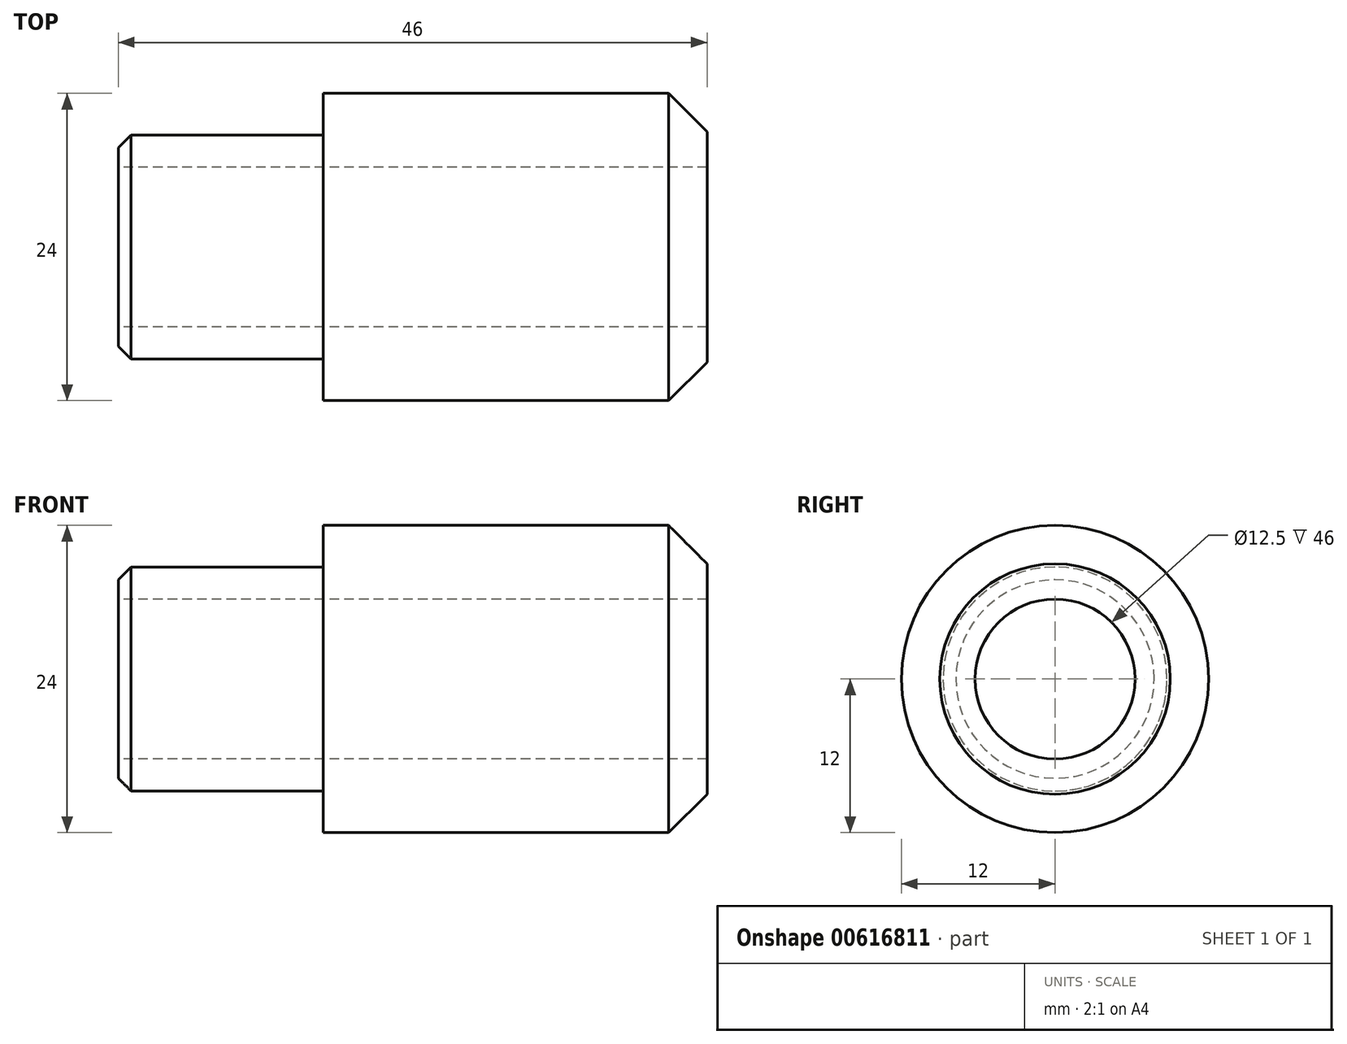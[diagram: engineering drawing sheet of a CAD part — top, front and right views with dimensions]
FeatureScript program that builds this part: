
annotation { "Feature Type Name" : "Feature", "Feature Type Description" : "" }
export const myFeature = defineFeature(function(context is Context, id is Id, definition is map)
    precondition{}
    {
        {
            var Q0;
            Q0=qCreatedBy(makeId("Front.planeOp"),FACE);
            var sketch = newSketch(context, id + "F0", { "sketchPlane" : qUnion([Q0])});
            skLineSegment(sketch, "E0", {"start": v(-46, 8.75) * mm, "end": v(-46, 6.25) * mm});
            skLineSegment(sketch, "E1", {"start": v(-46, 6.25) * mm, "end": v(0, 6.25) * mm});
            skLineSegment(sketch, "E2", {"start": v(0, 6.25) * mm, "end": v(0, 9) * mm});
            skLineSegment(sketch, "E3", {"start": v(0, 9) * mm, "end": v(-3, 12) * mm});
            skLineSegment(sketch, "E4", {"start": v(-3, 12) * mm, "end": v(-30, 12) * mm});
            skLineSegment(sketch, "E5", {"start": v(-30, 12) * mm, "end": v(-30, 8.75) * mm});
            skLineSegment(sketch, "E6", {"start": v(-30, 8.75) * mm, "end": v(-46, 8.75) * mm});
            skLineSegment(sketch, "E7", {"start": v(-82.92, 0) * mm, "end": v(0, 0) * mm, "construction": true});
            skSolve(sketch);
        }
        {
            var Q0;
            Q0=makeQuery(id+"F0.imprint","IMPRINT",FACE,{"disambiguationData":[TD([[makeQuery(id+"F0.imprint","IMPRINT",EDGE,{"derivedFrom":sQuery(id+"F0.wireOp",EDGE,"E0")}),1.0]])]});
            var Q1;
            Q1=sQuery(id+"F0.wireOp",EDGE,"E7");
            revolve(context, id + "F1", {"surfaceOperationType" : NewSurfaceOperationType.NEW, "entities" : qUnion([Q0]), "axis" : qUnion([Q1]), "revolveType" : RevolveType.FULL});
        }
        {
            var Q0;
            Q0=makeQuery(id+"F1.opRevolve","SWEPT_EDGE",EDGE,{"disambiguationData":[OSD([sQuery(id+"F0.wireOp",EDGE,"E0"),sQuery(id+"F0.wireOp",EDGE,"E6")])]});
            chamfer(context, id + "F2", {"entities" : qUnion([Q0]), "width" : 1 * mm, "tangentPropagation" : true});
        }
    });
